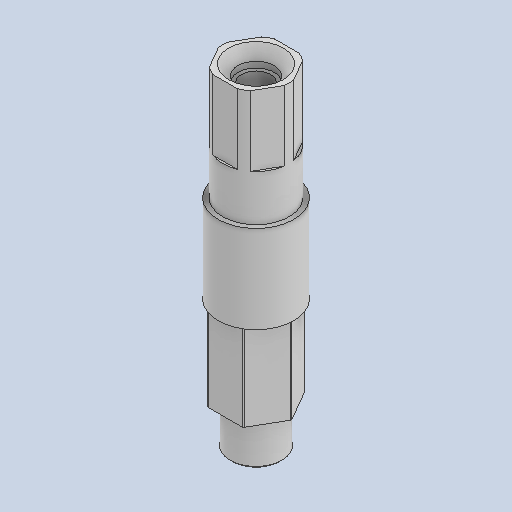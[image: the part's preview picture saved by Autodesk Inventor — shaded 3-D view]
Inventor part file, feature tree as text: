
AUTODESK INVENTOR PART (.ipt)
format: ipt  version: 2022.3 (Build 263350000, 350)  size: 126,976 bytes
history: native  units: in
note: dims shown in document units (in); Inventor stores cm internally (conversion verified against a paired STEP export)
features: fillet x1
ambient origin geometry x8: Origin, YZ Plane, XZ Plane, XY Plane, X Axis, Y Axis, Z Axis, Center Point
bodies: Solid1 (feature_tree)
feature tree (1):
  fillet  "Fillet1"  [1 undecoded]
note: 1 required parameter value undecoded (feature->parameter linkage not recoverable at this tier; creation-order binding heuristic only, values carry confidence <= 0.55)
